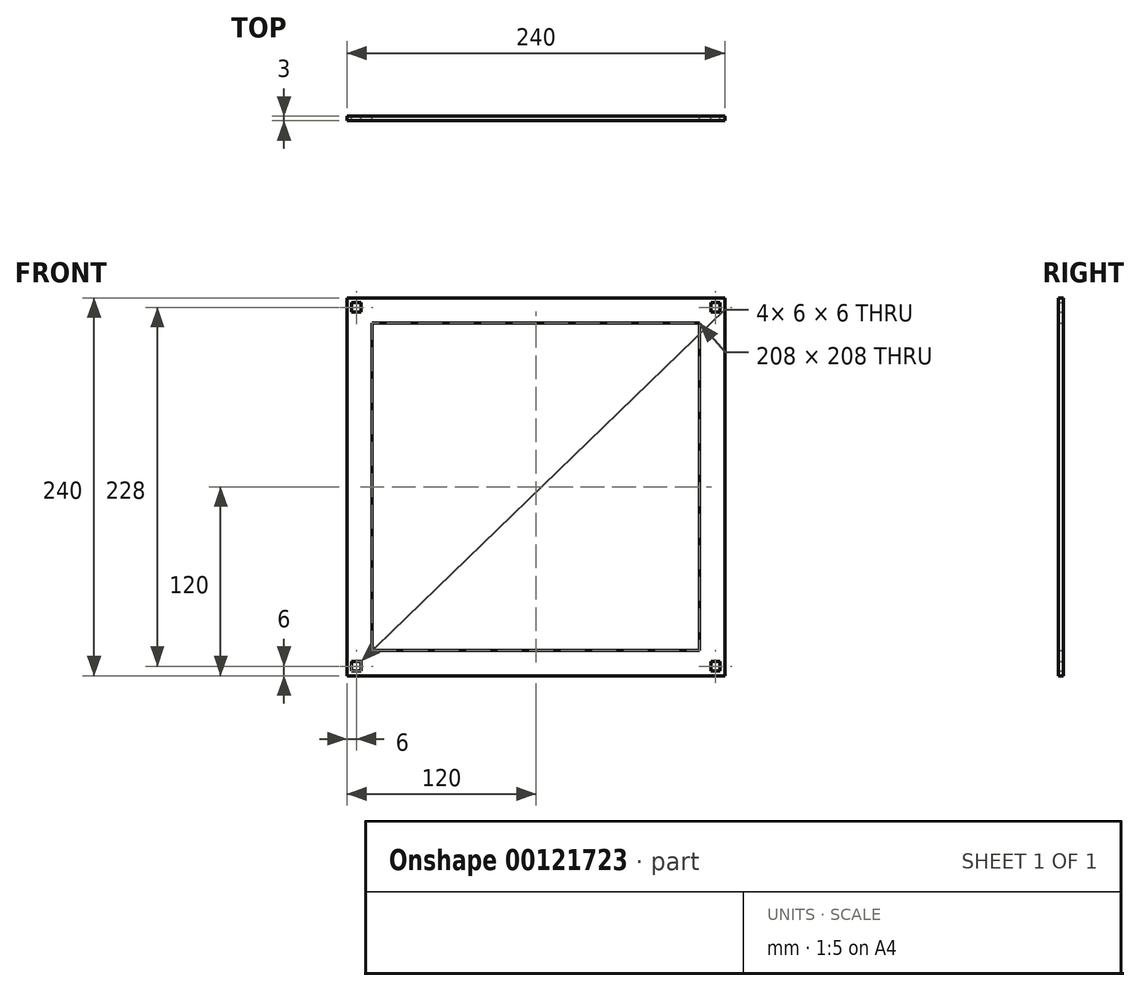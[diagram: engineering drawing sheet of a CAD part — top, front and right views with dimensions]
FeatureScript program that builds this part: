
annotation { "Feature Type Name" : "Feature", "Feature Type Description" : "" }
export const myFeature = defineFeature(function(context is Context, id is Id, definition is map)
    precondition{}
    {
        {
            assignVariable(context, id + "F0", {"name" : "thicknessWood", "anyValue" : 3});
        }
        {
            var Q0;
            Q0=qCreatedBy(makeId("Front.planeOp"),FACE);
            var sketch = newSketch(context, id + "F1", { "sketchPlane" : qUnion([Q0])});
            skLineSegment(sketch, "E0.bottom", {"start": v(0, 0) * mm, "end": v(240, 0) * mm});
            skLineSegment(sketch, "E0.top", {"start": v(0, 240) * mm, "end": v(240, 240) * mm});
            skLineSegment(sketch, "E0.left", {"start": v(0, 0) * mm, "end": v(0, 240) * mm});
            skLineSegment(sketch, "E0.right", {"start": v(240, 0) * mm, "end": v(240, 240) * mm});
            skLineSegment(sketch, "E1.bottom", {"start": v(16, 224) * mm, "end": v(224, 224) * mm});
            skLineSegment(sketch, "E1.top", {"start": v(16, 16) * mm, "end": v(224, 16) * mm});
            skLineSegment(sketch, "E1.left", {"start": v(16, 224) * mm, "end": v(16, 16) * mm});
            skLineSegment(sketch, "E1.right", {"start": v(224, 224) * mm, "end": v(224, 16) * mm});
            skLineSegment(sketch, "E2.bottom", {"start": v(9, 237) * mm, "end": v(3, 237) * mm});
            skLineSegment(sketch, "E2.top", {"start": v(9, 231) * mm, "end": v(3, 231) * mm});
            skLineSegment(sketch, "E2.left", {"start": v(9, 237) * mm, "end": v(9, 231) * mm});
            skLineSegment(sketch, "E2.right", {"start": v(3, 237) * mm, "end": v(3, 231) * mm});
            skLineSegment(sketch, "E3", {"start": v(120, 240) * mm, "end": v(120, 0) * mm, "construction": true});
            skLineSegment(sketch, "E4", {"start": v(0, 120) * mm, "end": v(240, 120) * mm, "construction": true});
            skSolve(sketch);
        }
        {
            var Q0;
            Q0=makeQuery(id+"F1.imprint","IMPRINT",FACE,{"disambiguationData":[TD([[makeQuery(id+"F1.imprint","IMPRINT",EDGE,{"derivedFrom":sQuery(id+"F1.wireOp",EDGE,"E0.bottom")}),1.0]])]});
            var Q1;
            Q1=makeQuery(id+"F1.imprint","IMPRINT",FACE,{"disambiguationData":[TD([[makeQuery(id+"F1.imprint","IMPRINT",EDGE,{"derivedFrom":sQuery(id+"F1.wireOp",EDGE,"E2.bottom")}),1.0]])]});
            var Q2;
            Q2=sQuery(id+"F1.wireOp",EDGE,"E1.left");
            extrude(context, id + "F2", {"entities" : qUnion([Q0, Q1]), "surfaceEntities" : qUnion([Q2]), "depth" : (getVariable(context, 'thicknessWood')) * mm});
        }
        {
            var Q0;
            Q0=makeQuery(id+"F1.imprint","IMPRINT",FACE,{"disambiguationData":[TD([[makeQuery(id+"F1.imprint","IMPRINT",EDGE,{"derivedFrom":sQuery(id+"F1.wireOp",EDGE,"E2.bottom")}),1.0]])]});
            extrude(context, id + "F3", {"entities" : qUnion([Q0]), "operationType" : NewBodyOperationType.REMOVE, "depth" : 25 * mm});
        }
        {
            var Q0;
            Q0=makeQuery(id+"F2.opExtrude","SWEPT_FACE",FACE,{"disambiguationData":[OSD([sQuery(id+"F1.wireOp",EDGE,"E0.left")])]});
            var Q1;
            Q1=makeQuery(id+"F2.opExtrude","SWEPT_FACE",FACE,{"disambiguationData":[OSD([sQuery(id+"F1.wireOp",EDGE,"E0.right")])]});
            cPlane(context, id + "F4", {"entities" : qUnion([Q0, Q1]), "cplaneType" : CPlaneType.MID_PLANE, "offset" : 25 * mm, "width" : 150 * mm, "height" : 150 * mm});
        }
        {
            var Q0;
            Q0=makeQuery(id+"F2.opExtrude","SWEPT_BODY",BODY,{"disambiguationData":[OSD([sQuery(id+"F1.wireOp",EDGE,"E0.bottom"),sQuery(id+"F1.wireOp",EDGE,"E0.top"),sQuery(id+"F1.wireOp",EDGE,"E0.left"),sQuery(id+"F1.wireOp",EDGE,"E0.right"),sQuery(id+"F1.wireOp",EDGE,"E1.bottom"),sQuery(id+"F1.wireOp",EDGE,"E1.top"),sQuery(id+"F1.wireOp",EDGE,"E1.left"),sQuery(id+"F1.wireOp",EDGE,"E1.right")])]});
            var Q1;
            Q1=qCreatedBy(id+"F4.planeOp",FACE);
            mirror(context, id + "F5", {"operationType" : NewBodyOperationType.INTERSECT, "entities" : qUnion([Q0]), "mirrorPlane" : qUnion([Q1])});
        }
        {
            var Q0;
            Q0=makeQuery(id+"F2.opExtrude","SWEPT_FACE",FACE,{"disambiguationData":[OSD([sQuery(id+"F1.wireOp",EDGE,"E0.top")])]});
            var Q1;
            Q1=makeQuery(id+"F2.opExtrude","SWEPT_FACE",FACE,{"disambiguationData":[OSD([sQuery(id+"F1.wireOp",EDGE,"E0.bottom")])]});
            cPlane(context, id + "F6", {"entities" : qUnion([Q0, Q1]), "cplaneType" : CPlaneType.MID_PLANE, "offset" : 25 * mm, "width" : 150 * mm, "height" : 150 * mm});
        }
        {
            var Q0;
            Q0=makeQuery(id+"F2.opExtrude","SWEPT_BODY",BODY,{"disambiguationData":[OSD([sQuery(id+"F1.wireOp",EDGE,"E0.bottom"),sQuery(id+"F1.wireOp",EDGE,"E0.top"),sQuery(id+"F1.wireOp",EDGE,"E0.left"),sQuery(id+"F1.wireOp",EDGE,"E0.right"),sQuery(id+"F1.wireOp",EDGE,"E1.bottom"),sQuery(id+"F1.wireOp",EDGE,"E1.top"),sQuery(id+"F1.wireOp",EDGE,"E1.left"),sQuery(id+"F1.wireOp",EDGE,"E1.right")])]});
            var Q1;
            Q1=qCreatedBy(id+"F6.planeOp",FACE);
            mirror(context, id + "F7", {"operationType" : NewBodyOperationType.INTERSECT, "entities" : qUnion([Q0]), "mirrorPlane" : qUnion([Q1])});
        }
    });
